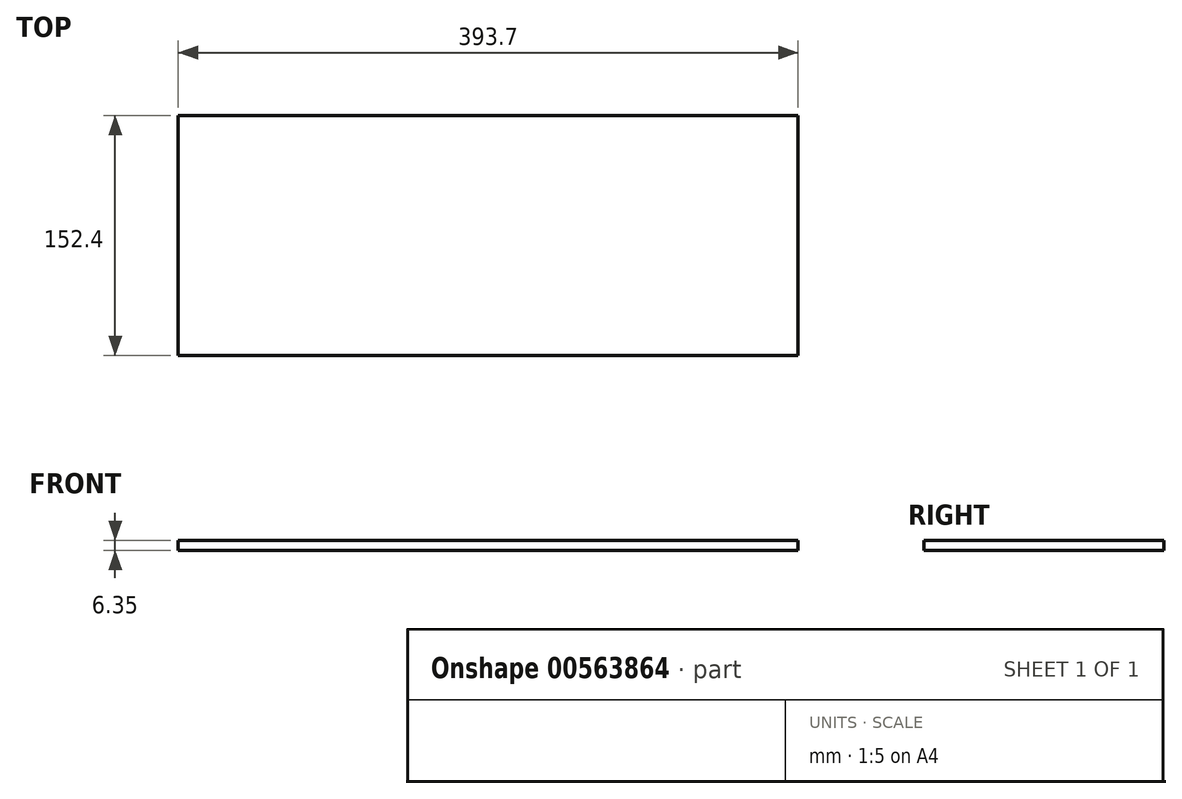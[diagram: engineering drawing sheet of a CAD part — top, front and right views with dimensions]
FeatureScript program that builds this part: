
annotation { "Feature Type Name" : "Feature", "Feature Type Description" : "" }
export const myFeature = defineFeature(function(context is Context, id is Id, definition is map)
    precondition{}
    {
        {
            var Q0;
            Q0=qCreatedBy(makeId("Top.planeOp"),FACE);
            var sketch = newSketch(context, id + "F0", { "sketchPlane" : qUnion([Q0])});
            skLineSegment(sketch, "E0", {"start": v(0, 0) * mm, "end": v(393.7, 0) * mm});
            skLineSegment(sketch, "E1", {"start": v(0, 0) * mm, "end": v(0, 152.4) * mm});
            skLineSegment(sketch, "E2", {"start": v(0, 152.4) * mm, "end": v(393.7, 152.4) * mm});
            skLineSegment(sketch, "E3", {"start": v(393.7, 152.4) * mm, "end": v(393.7, 0) * mm});
            skSolve(sketch);
        }
        {
            var Q0;
            Q0=makeQuery(id+"F0.imprint","IMPRINT",FACE,{"disambiguationData":[TD([[makeQuery(id+"F0.imprint","IMPRINT",EDGE,{"derivedFrom":sQuery(id+"F0.wireOp",EDGE,"E0")}),1.0]])]});
            extrude(context, id + "F1", {"entities" : qUnion([Q0]), "depth" : 6.35 * mm, "offsetDistance" : 25.4 * mm});
        }
    });
